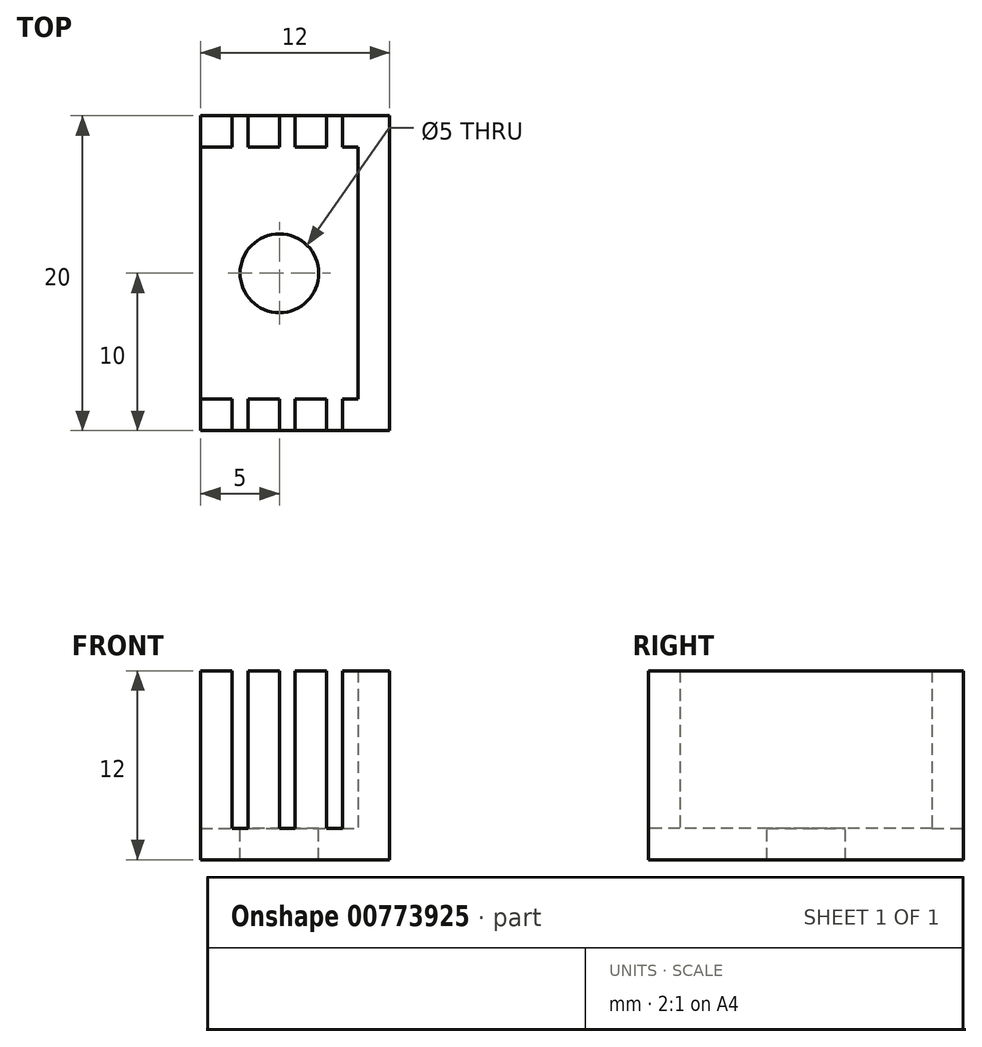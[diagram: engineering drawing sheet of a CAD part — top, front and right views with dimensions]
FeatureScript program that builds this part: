
annotation { "Feature Type Name" : "Feature", "Feature Type Description" : "" }
export const myFeature = defineFeature(function(context is Context, id is Id, definition is map)
    precondition{}
    {
        {
            var Q0;
            Q0=qCreatedBy(makeId("Top.planeOp"),FACE);
            var sketch = newSketch(context, id + "F0", { "sketchPlane" : qUnion([Q0])});
            skLineSegment(sketch, "E0.bottom", {"start": v(-12, 0) * mm, "end": v(0, 0) * mm});
            skLineSegment(sketch, "E0.top", {"start": v(-12, 20) * mm, "end": v(0, 20) * mm});
            skLineSegment(sketch, "E0.left", {"start": v(-12, 0) * mm, "end": v(-12, 20) * mm});
            skLineSegment(sketch, "E0.right", {"start": v(0, 0) * mm, "end": v(0, 20) * mm});
            skSolve(sketch);
        }
        {
            var Q0;
            Q0 = qSketchRegion(id + "F0", true);
            extrude(context, id + "F1", {"entities" : qUnion([Q0]), "depth" : 2 * mm, "offsetDistance" : 25 * mm});
        }
        {
            var Q0;
            Q0=makeQuery(id+"F1.opExtrude","CAP_FACE",FACE,{"disambiguationData":[OSD([sQuery(id+"F0.wireOp",EDGE,"E0.bottom"),sQuery(id+"F0.wireOp",EDGE,"E0.top"),sQuery(id+"F0.wireOp",EDGE,"E0.left"),sQuery(id+"F0.wireOp",EDGE,"E0.right")])],"isStart":false});
            var sketch = newSketch(context, id + "F2", { "sketchPlane" : qUnion([Q0])});
            skLineSegment(sketch, "E1.bottom", {"start": v(-12, 20) * mm, "end": v(-10, 20) * mm});
            skLineSegment(sketch, "E1.top", {"start": v(-12, 18) * mm, "end": v(-10, 18) * mm});
            skLineSegment(sketch, "E1.left", {"start": v(-12, 20) * mm, "end": v(-12, 18) * mm});
            skLineSegment(sketch, "E1.right", {"start": v(-10, 20) * mm, "end": v(-10, 18) * mm});
            skLineSegment(sketch, "E2.bottom", {"start": v(-9, 20) * mm, "end": v(0, 20) * mm});
            skLineSegment(sketch, "E2.left", {"start": v(-9, 20) * mm, "end": v(-9, 18) * mm});
            skLineSegment(sketch, "E2.right", {"start": v(0, 20) * mm, "end": v(0, 18) * mm});
            skLineSegment(sketch, "E3", {"start": v(-12, 10) * mm, "end": v(0, 10) * mm});
            skLineSegment(sketch, "E4.MirrorCS", {"start": v(-10, 0) * mm, "end": v(-10, 2) * mm});
            skLineSegment(sketch, "E5.MirrorCS", {"start": v(-12, 2) * mm, "end": v(-10, 2) * mm});
            skLineSegment(sketch, "E6.MirrorCS", {"start": v(-12, 0) * mm, "end": v(-12, 2) * mm});
            skLineSegment(sketch, "E7.MirrorCS", {"start": v(-9, 0) * mm, "end": v(-9, 2) * mm});
            skLineSegment(sketch, "E8.bottom", {"start": v(-2, 18) * mm, "end": v(0, 18) * mm});
            skLineSegment(sketch, "E8.top", {"start": v(-2, 2) * mm, "end": v(0, 2) * mm});
            skLineSegment(sketch, "E8.left", {"start": v(-2, 18) * mm, "end": v(-2, 2) * mm});
            skLineSegment(sketch, "E8.right", {"start": v(0, 18) * mm, "end": v(0, 2) * mm});
            skLineSegment(sketch, "E9", {"start": v(-7, 18) * mm, "end": v(-7, 20) * mm});
            skLineSegment(sketch, "E10", {"start": v(-6, 18) * mm, "end": v(-6, 20) * mm});
            skLineSegment(sketch, "E11", {"start": v(-3, 18) * mm, "end": v(-3, 20) * mm});
            skLineSegment(sketch, "E12", {"start": v(-9, 18) * mm, "end": v(-7, 18) * mm});
            skLineSegment(sketch, "E13", {"start": v(-6, 18) * mm, "end": v(-4, 18) * mm});
            skLineSegment(sketch, "E14", {"start": v(-3, 18) * mm, "end": v(-2, 18) * mm});
            skLineSegment(sketch, "E15", {"start": v(-4, 18) * mm, "end": v(-4, 20) * mm});
            skLineSegment(sketch, "E16.MirrorCS", {"start": v(-7, 2) * mm, "end": v(-7, 0) * mm});
            skLineSegment(sketch, "E17.MirrorCS", {"start": v(-6, 2) * mm, "end": v(-6, 0) * mm});
            skLineSegment(sketch, "E18.MirrorCS", {"start": v(-4, 2) * mm, "end": v(-4, 0) * mm});
            skLineSegment(sketch, "E19.MirrorCS", {"start": v(-3, 2) * mm, "end": v(-3, 0) * mm});
            skLineSegment(sketch, "E20", {"start": v(-9, 2) * mm, "end": v(-7, 2) * mm});
            skLineSegment(sketch, "E21", {"start": v(-6, 2) * mm, "end": v(-4, 2) * mm});
            skLineSegment(sketch, "E22", {"start": v(-3, 2) * mm, "end": v(-2, 2) * mm});
            skSolve(sketch);
        }
        {
            var Q0;
            Q0 = qSketchRegion(id + "F2", true);
            var Q1;
            {var subQ0=sQuery(id+"F2.wireOp",EDGE,"E4.MirrorCS");Q1=makeQuery(id+"F2.imprint","IMPRINT",FACE,{"disambiguationData":[TD([[makeQuery(id+"F2.imprint","IMPRINT",EDGE,{"derivedFrom":subQ0}),1.0]])]});}
            var Q2;
            {var subQ4=sQuery(id+"F2.wireOp",EDGE,"E7.MirrorCS");Q2=makeQuery(id+"F2.imprint","IMPRINT",FACE,{"disambiguationData":[TD([[makeQuery(id+"F2.imprint","IMPRINT",EDGE,{"derivedFrom":subQ4}),-1.0]])]});}
            extrude(context, id + "F3", {"entities" : qUnion([Q0, Q1, Q2]), "operationType" : NewBodyOperationType.ADD, "depth" : 10 * mm, "offsetDistance" : 25 * mm});
        }
        {
            var Q0;
            Q0=makeQuery(id+"F1.opExtrude","CAP_FACE",FACE,{"disambiguationData":[OSD([sQuery(id+"F0.wireOp",EDGE,"E0.bottom"),sQuery(id+"F0.wireOp",EDGE,"E0.top"),sQuery(id+"F0.wireOp",EDGE,"E0.left"),sQuery(id+"F0.wireOp",EDGE,"E0.right")])],"isStart":false});
            var sketch = newSketch(context, id + "F4", { "sketchPlane" : qUnion([Q0])});
            skCircle(sketch, "E23", {"center": v(-7, 10) * mm, "radius": 2.5 * mm});
            skSolve(sketch);
        }
        {
            var Q0;
            Q0 = qSketchRegion(id + "F4", true);
            extrude(context, id + "F5", {"entities" : qUnion([Q0]), "operationType" : NewBodyOperationType.REMOVE, "oppositeDirection" : true, "depth" : 25 * mm, "offsetDistance" : 25 * mm});
        }
        {
            var Q0;
            {var subQ0=sQuery(id+"F2.wireOp",EDGE,"E17.MirrorCS");Q0=makeQuery(id+"F2.imprint","IMPRINT",FACE,{"disambiguationData":[TD([[makeQuery(id+"F2.imprint","IMPRINT",EDGE,{"derivedFrom":subQ0}),1.0]])]});}
            var Q1;
            {var subQ3=sQuery(id+"F2.wireOp",EDGE,"E8.top");Q1=makeQuery(id+"F2.imprint","IMPRINT",FACE,{"disambiguationData":[TD([[makeQuery(id+"F2.imprint","IMPRINT",EDGE,{"derivedFrom":subQ3}),-1.0]])]});}
            extrude(context, id + "F6", {"entities" : qUnion([Q0, Q1]), "operationType" : NewBodyOperationType.ADD, "depth" : 10 * mm, "offsetDistance" : 25 * mm});
        }
    });
